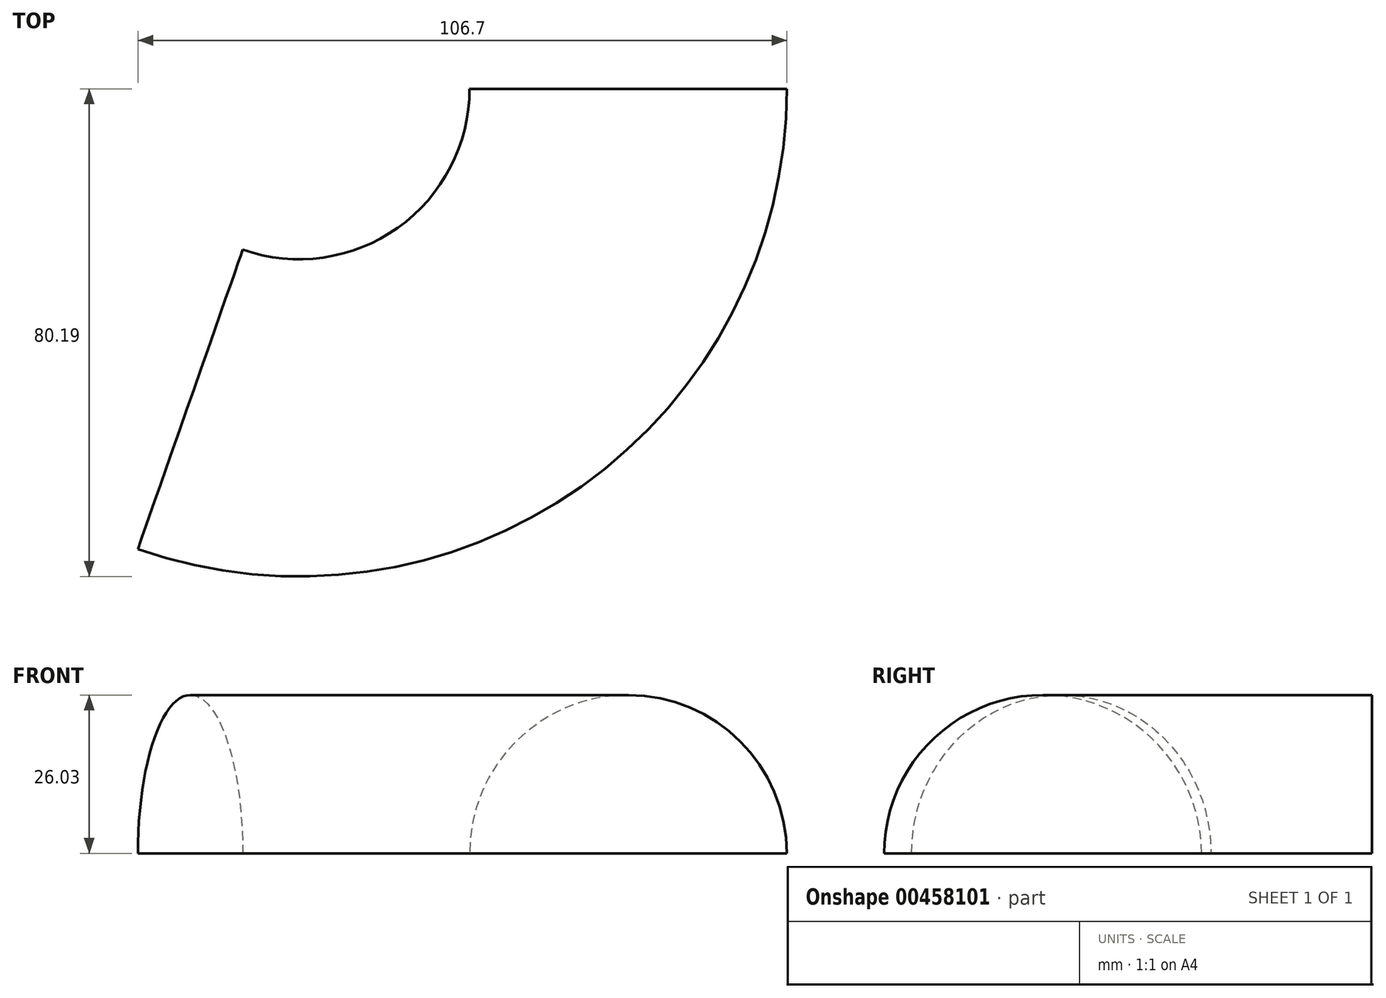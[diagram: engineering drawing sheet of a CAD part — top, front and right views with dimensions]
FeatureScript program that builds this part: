
annotation { "Feature Type Name" : "Feature", "Feature Type Description" : "" }
export const myFeature = defineFeature(function(context is Context, id is Id, definition is map)
    precondition{}
    {
        {
            var Q0;
            Q0=qCreatedBy(makeId("Front.planeOp"),FACE);
            var sketch = newSketch(context, id + "F0", { "sketchPlane" : qUnion([Q0])});
            skLineSegment(sketch, "E0", {"start": v(-26.92, 0) * mm, "end": v(25.26, 0) * mm});
            skArc(sketch, "E1", {"start": v(25.26, 0) * mm, "mid": v(-0.83, 26.03) * mm, "end": v(-26.92, 0) * mm});
            skSolve(sketch);
        }
        {
            var Q0;
            Q0=qCreatedBy(makeId("Top.planeOp"),FACE);
            var sketch = newSketch(context, id + "F1", { "sketchPlane" : qUnion([Q0])});
            skArc(sketch, "E2", {"start": v(0, 0) * mm, "mid": v(-23.15, -44.8) * mm, "end": v(-73.1, -51.85) * mm});
            skSolve(sketch);
        }
        {
            var Q0;
            Q0=makeQuery(id+"F0.imprint","IMPRINT",FACE,{"disambiguationData":[TD([[makeQuery(id+"F0.imprint","IMPRINT",EDGE,{"derivedFrom":sQuery(id+"F0.wireOp",EDGE,"E0")}),1.0]])]});
            var Q1;
            Q1=sQuery(id+"F1.wireOp",EDGE,"E2");
            sweep(context, id + "F2", {"profiles" : qUnion([Q0]), "path" : qUnion([Q1])});
        }
    });
